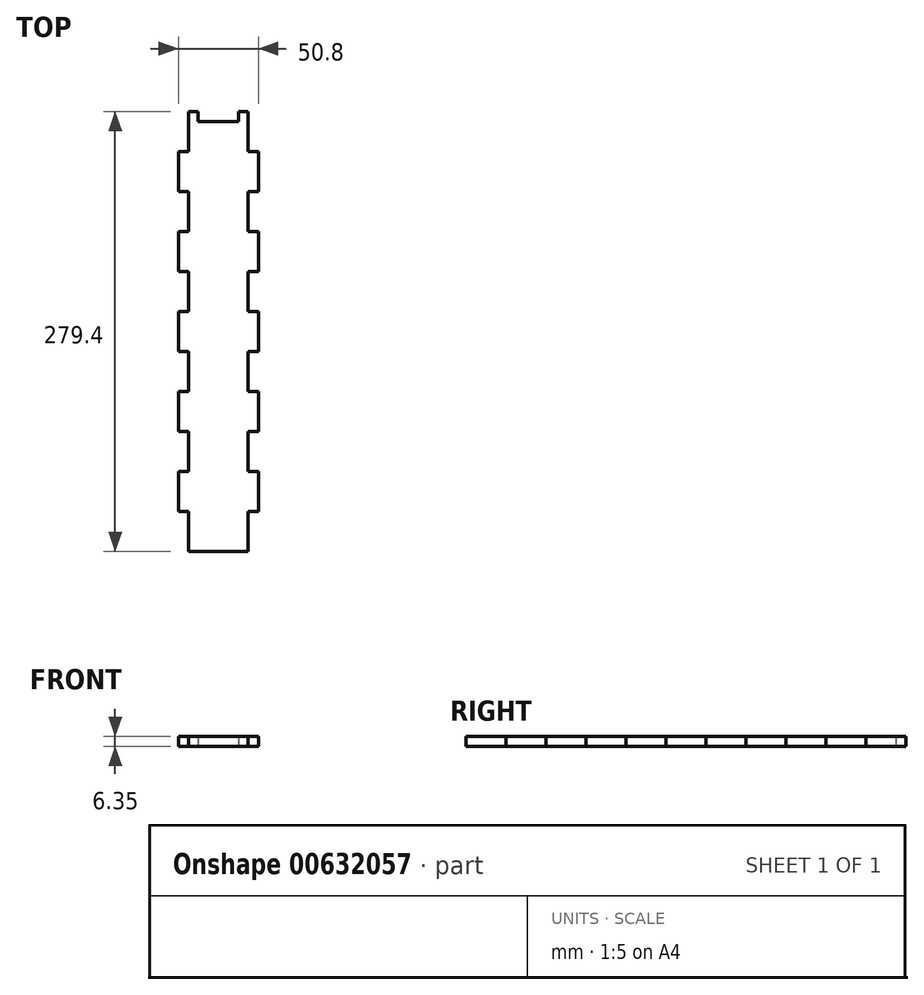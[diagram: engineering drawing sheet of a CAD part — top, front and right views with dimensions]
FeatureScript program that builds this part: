
annotation { "Feature Type Name" : "Feature", "Feature Type Description" : "" }
export const myFeature = defineFeature(function(context is Context, id is Id, definition is map)
    precondition{}
    {
        {
            var Q0;
            Q0=qCreatedBy(makeId("Top.planeOp"),FACE);
            var sketch = newSketch(context, id + "F0", { "sketchPlane" : qUnion([Q0])});
            skLineSegment(sketch, "E0.bottom", {"start": v(0, 279.4) * mm, "end": v(38.1, 279.4) * mm});
            skLineSegment(sketch, "E0.top", {"start": v(0, 0) * mm, "end": v(38.1, 0) * mm});
            skLineSegment(sketch, "E0.left", {"start": v(0, 279.4) * mm, "end": v(0, 0) * mm});
            skLineSegment(sketch, "E0.right", {"start": v(38.1, 279.4) * mm, "end": v(38.1, 0) * mm});
            skSolve(sketch);
        }
        {
            var Q0;
            Q0=qSketchRegion(id+"F0",true);
            extrude(context, id + "F1", {"entities" : qUnion([Q0]), "depth" : 6.35 * mm, "offsetDistance" : 25.4 * mm});
        }
        {
            var Q0;
            Q0=makeQuery(id+"F1.opExtrude","SWEPT_FACE",FACE,{"disambiguationData":[OSD([sQuery(id+"F0.wireOp",EDGE,"E0.right")])]});
            var sketch = newSketch(context, id + "F2", { "sketchPlane" : qUnion([Q0])});
            skLineSegment(sketch, "E1.bottom", {"start": v(0, 6.35) * mm, "end": v(25.4, 6.35) * mm});
            skLineSegment(sketch, "E1.top", {"start": v(0, 0) * mm, "end": v(25.4, 0) * mm});
            skLineSegment(sketch, "E1.left", {"start": v(0, 6.35) * mm, "end": v(0, 0) * mm});
            skLineSegment(sketch, "E1.right", {"start": v(25.4, 6.35) * mm, "end": v(25.4, 0) * mm});
            skLineSegment(sketch, "E2.bottom", {"start": v(25.4, 6.35) * mm, "end": v(50.8, 6.35) * mm});
            skLineSegment(sketch, "E2.top", {"start": v(25.4, 0) * mm, "end": v(50.8, 0) * mm});
            skLineSegment(sketch, "E2.right", {"start": v(50.8, 6.35) * mm, "end": v(50.8, 0) * mm});
            skLineSegment(sketch, "E3.bottom", {"start": v(50.8, 6.35) * mm, "end": v(76.2, 6.35) * mm});
            skLineSegment(sketch, "E3.top", {"start": v(50.8, 0) * mm, "end": v(76.2, 0) * mm});
            skLineSegment(sketch, "E3.right", {"start": v(76.2, 6.35) * mm, "end": v(76.2, 0) * mm});
            skLineSegment(sketch, "E4.bottom", {"start": v(76.2, 6.35) * mm, "end": v(101.6, 6.35) * mm});
            skLineSegment(sketch, "E4.top", {"start": v(76.2, 0) * mm, "end": v(101.6, 0) * mm});
            skLineSegment(sketch, "E4.right", {"start": v(101.6, 6.35) * mm, "end": v(101.6, 0) * mm});
            skLineSegment(sketch, "E5.bottom", {"start": v(101.6, 6.35) * mm, "end": v(127, 6.35) * mm});
            skLineSegment(sketch, "E5.top", {"start": v(101.6, 0) * mm, "end": v(127, 0) * mm});
            skLineSegment(sketch, "E5.right", {"start": v(127, 6.35) * mm, "end": v(127, 0) * mm});
            skLineSegment(sketch, "E6.bottom", {"start": v(127, 6.35) * mm, "end": v(152.4, 6.35) * mm});
            skLineSegment(sketch, "E6.top", {"start": v(127, 0) * mm, "end": v(152.4, 0) * mm});
            skLineSegment(sketch, "E6.right", {"start": v(152.4, 6.35) * mm, "end": v(152.4, 0) * mm});
            skLineSegment(sketch, "E7.bottom", {"start": v(152.4, 6.35) * mm, "end": v(177.8, 6.35) * mm});
            skLineSegment(sketch, "E7.top", {"start": v(152.4, 0) * mm, "end": v(177.8, 0) * mm});
            skLineSegment(sketch, "E7.right", {"start": v(177.8, 6.35) * mm, "end": v(177.8, 0) * mm});
            skLineSegment(sketch, "E8.bottom", {"start": v(177.8, 6.35) * mm, "end": v(203.2, 6.35) * mm});
            skLineSegment(sketch, "E8.top", {"start": v(177.8, 0) * mm, "end": v(203.2, 0) * mm});
            skLineSegment(sketch, "E8.right", {"start": v(203.2, 6.35) * mm, "end": v(203.2, 0) * mm});
            skLineSegment(sketch, "E9.bottom", {"start": v(203.2, 6.35) * mm, "end": v(228.6, 6.35) * mm});
            skLineSegment(sketch, "E9.top", {"start": v(203.2, 0) * mm, "end": v(228.6, 0) * mm});
            skLineSegment(sketch, "E9.right", {"start": v(228.6, 6.35) * mm, "end": v(228.6, 0) * mm});
            skLineSegment(sketch, "E10.bottom", {"start": v(228.6, 6.35) * mm, "end": v(254, 6.35) * mm});
            skLineSegment(sketch, "E10.top", {"start": v(228.6, 0) * mm, "end": v(254, 0) * mm});
            skLineSegment(sketch, "E10.right", {"start": v(254, 6.35) * mm, "end": v(254, 0) * mm});
            skLineSegment(sketch, "E11.bottom", {"start": v(254, 6.35) * mm, "end": v(279.4, 6.35) * mm});
            skLineSegment(sketch, "E11.top", {"start": v(254, 0) * mm, "end": v(279.4, 0) * mm});
            skLineSegment(sketch, "E11.right", {"start": v(279.4, 6.35) * mm, "end": v(279.4, 0) * mm});
            skSolve(sketch);
        }
        {
            var Q0;
            Q0=makeQuery(id+"F1.opExtrude","SWEPT_FACE",FACE,{"disambiguationData":[OSD([sQuery(id+"F0.wireOp",EDGE,"E0.left")])]});
            var sketch = newSketch(context, id + "F3", { "sketchPlane" : qUnion([Q0])});
            skLineSegment(sketch, "E12.bottom", {"start": v(-279.4, 6.35) * mm, "end": v(-254, 6.35) * mm});
            skLineSegment(sketch, "E12.top", {"start": v(-279.4, 0) * mm, "end": v(-254, 0) * mm});
            skLineSegment(sketch, "E12.left", {"start": v(-279.4, 6.35) * mm, "end": v(-279.4, 0) * mm});
            skLineSegment(sketch, "E12.right", {"start": v(-254, 6.35) * mm, "end": v(-254, 0) * mm});
            skLineSegment(sketch, "E13.bottom", {"start": v(-254, 6.35) * mm, "end": v(-228.6, 6.35) * mm});
            skLineSegment(sketch, "E13.top", {"start": v(-254, 0) * mm, "end": v(-228.6, 0) * mm});
            skLineSegment(sketch, "E13.right", {"start": v(-228.6, 6.35) * mm, "end": v(-228.6, 0) * mm});
            skLineSegment(sketch, "E14.bottom", {"start": v(-228.6, 6.35) * mm, "end": v(-203.2, 6.35) * mm});
            skLineSegment(sketch, "E14.top", {"start": v(-228.6, 0) * mm, "end": v(-203.2, 0) * mm});
            skLineSegment(sketch, "E14.right", {"start": v(-203.2, 6.35) * mm, "end": v(-203.2, 0) * mm});
            skLineSegment(sketch, "E15.bottom", {"start": v(-203.2, 6.35) * mm, "end": v(-177.8, 6.35) * mm});
            skLineSegment(sketch, "E15.top", {"start": v(-203.2, 0) * mm, "end": v(-177.8, 0) * mm});
            skLineSegment(sketch, "E15.right", {"start": v(-177.8, 6.35) * mm, "end": v(-177.8, 0) * mm});
            skLineSegment(sketch, "E16.bottom", {"start": v(-177.8, 6.35) * mm, "end": v(-152.4, 6.35) * mm});
            skLineSegment(sketch, "E16.top", {"start": v(-177.8, 0) * mm, "end": v(-152.4, 0) * mm});
            skLineSegment(sketch, "E16.right", {"start": v(-152.4, 6.35) * mm, "end": v(-152.4, 0) * mm});
            skLineSegment(sketch, "E17.bottom", {"start": v(-152.4, 6.35) * mm, "end": v(-127, 6.35) * mm});
            skLineSegment(sketch, "E17.top", {"start": v(-152.4, 0) * mm, "end": v(-127, 0) * mm});
            skLineSegment(sketch, "E17.right", {"start": v(-127, 6.35) * mm, "end": v(-127, 0) * mm});
            skLineSegment(sketch, "E18.bottom", {"start": v(-127, 6.35) * mm, "end": v(-101.6, 6.35) * mm});
            skLineSegment(sketch, "E18.top", {"start": v(-127, 0) * mm, "end": v(-101.6, 0) * mm});
            skLineSegment(sketch, "E18.right", {"start": v(-101.6, 6.35) * mm, "end": v(-101.6, 0) * mm});
            skLineSegment(sketch, "E19.bottom", {"start": v(-101.6, 6.35) * mm, "end": v(-76.2, 6.35) * mm});
            skLineSegment(sketch, "E19.top", {"start": v(-101.6, 0) * mm, "end": v(-76.2, 0) * mm});
            skLineSegment(sketch, "E19.right", {"start": v(-76.2, 6.35) * mm, "end": v(-76.2, 0) * mm});
            skLineSegment(sketch, "E20.bottom", {"start": v(-76.2, 6.35) * mm, "end": v(-50.8, 6.35) * mm});
            skLineSegment(sketch, "E20.top", {"start": v(-76.2, 0) * mm, "end": v(-50.8, 0) * mm});
            skLineSegment(sketch, "E20.right", {"start": v(-50.8, 6.35) * mm, "end": v(-50.8, 0) * mm});
            skLineSegment(sketch, "E21.bottom", {"start": v(-50.8, 6.35) * mm, "end": v(-25.4, 6.35) * mm});
            skLineSegment(sketch, "E21.top", {"start": v(-50.8, 0) * mm, "end": v(-25.4, 0) * mm});
            skLineSegment(sketch, "E21.right", {"start": v(-25.4, 6.35) * mm, "end": v(-25.4, 0) * mm});
            skLineSegment(sketch, "E22.bottom", {"start": v(-25.4, 6.35) * mm, "end": v(0, 6.35) * mm});
            skLineSegment(sketch, "E22.top", {"start": v(-25.4, 0) * mm, "end": v(0, 0) * mm});
            skLineSegment(sketch, "E22.right", {"start": v(0, 6.35) * mm, "end": v(0, 0) * mm});
            skSolve(sketch);
        }
        {
            var Q0;
            Q0=makeQuery(id+"F2.imprint","IMPRINT",FACE,{"disambiguationData":[TD([[makeQuery(id+"F2.imprint","IMPRINT",EDGE,{"derivedFrom":sQuery(id+"F2.wireOp",EDGE,"E10.bottom")}),1.0]])]});
            var Q1;
            Q1=makeQuery(id+"F2.imprint","IMPRINT",FACE,{"disambiguationData":[TD([[makeQuery(id+"F2.imprint","IMPRINT",EDGE,{"derivedFrom":sQuery(id+"F2.wireOp",EDGE,"E8.bottom")}),1.0]])]});
            var Q2;
            Q2=makeQuery(id+"F2.imprint","IMPRINT",FACE,{"disambiguationData":[TD([[makeQuery(id+"F2.imprint","IMPRINT",EDGE,{"derivedFrom":sQuery(id+"F2.wireOp",EDGE,"E6.bottom")}),1.0]])]});
            var Q3;
            Q3=makeQuery(id+"F2.imprint","IMPRINT",FACE,{"disambiguationData":[TD([[makeQuery(id+"F2.imprint","IMPRINT",EDGE,{"derivedFrom":sQuery(id+"F2.wireOp",EDGE,"E4.bottom")}),1.0]])]});
            var Q4;
            Q4=makeQuery(id+"F2.imprint","IMPRINT",FACE,{"disambiguationData":[TD([[makeQuery(id+"F2.imprint","IMPRINT",EDGE,{"derivedFrom":sQuery(id+"F2.wireOp",EDGE,"E2.bottom")}),1.0]])]});
            extrude(context, id + "F4", {"entities" : qUnion([Q0, Q1, Q2, Q3, Q4]), "operationType" : NewBodyOperationType.ADD, "depth" : 6.35 * mm, "offsetDistance" : 25.4 * mm});
        }
        {
            var Q0;
            Q0=makeQuery(id+"F3.imprint","IMPRINT",FACE,{"disambiguationData":[TD([[makeQuery(id+"F3.imprint","IMPRINT",EDGE,{"derivedFrom":sQuery(id+"F3.wireOp",EDGE,"E21.bottom")}),-1.0]])]});
            var Q1;
            Q1=makeQuery(id+"F3.imprint","IMPRINT",FACE,{"disambiguationData":[TD([[makeQuery(id+"F3.imprint","IMPRINT",EDGE,{"derivedFrom":sQuery(id+"F3.wireOp",EDGE,"E19.bottom")}),-1.0]])]});
            var Q2;
            Q2=makeQuery(id+"F3.imprint","IMPRINT",FACE,{"disambiguationData":[TD([[makeQuery(id+"F3.imprint","IMPRINT",EDGE,{"derivedFrom":sQuery(id+"F3.wireOp",EDGE,"E17.bottom")}),-1.0]])]});
            var Q3;
            Q3=makeQuery(id+"F3.imprint","IMPRINT",FACE,{"disambiguationData":[TD([[makeQuery(id+"F3.imprint","IMPRINT",EDGE,{"derivedFrom":sQuery(id+"F3.wireOp",EDGE,"E15.bottom")}),-1.0]])]});
            var Q4;
            Q4=makeQuery(id+"F3.imprint","IMPRINT",FACE,{"disambiguationData":[TD([[makeQuery(id+"F3.imprint","IMPRINT",EDGE,{"derivedFrom":sQuery(id+"F3.wireOp",EDGE,"E13.bottom")}),-1.0]])]});
            extrude(context, id + "F5", {"entities" : qUnion([Q0, Q1, Q2, Q3, Q4]), "operationType" : NewBodyOperationType.ADD, "depth" : 6.35 * mm, "offsetDistance" : 25.4 * mm});
        }
        {
            var Q0;
            Q0=makeQuery(id+"F1.opExtrude","SWEPT_FACE",FACE,{"disambiguationData":[OSD([sQuery(id+"F0.wireOp",EDGE,"E0.bottom")])]});
            var sketch = newSketch(context, id + "F6", { "sketchPlane" : qUnion([Q0])});
            skLineSegment(sketch, "E23.bottom", {"start": v(-38.1, 6.35) * mm, "end": v(-31.75, 6.35) * mm});
            skLineSegment(sketch, "E23.top", {"start": v(-38.1, 0) * mm, "end": v(-31.75, 0) * mm});
            skLineSegment(sketch, "E23.left", {"start": v(-38.1, 6.35) * mm, "end": v(-38.1, 0) * mm});
            skLineSegment(sketch, "E23.right", {"start": v(-31.75, 6.35) * mm, "end": v(-31.75, 0) * mm});
            skLineSegment(sketch, "E24.bottom", {"start": v(0, 6.35) * mm, "end": v(-6.35, 6.35) * mm});
            skLineSegment(sketch, "E24.top", {"start": v(0, 0) * mm, "end": v(-6.35, 0) * mm});
            skLineSegment(sketch, "E24.left", {"start": v(0, 6.35) * mm, "end": v(0, 0) * mm});
            skLineSegment(sketch, "E24.right", {"start": v(-6.35, 6.35) * mm, "end": v(-6.35, 0) * mm});
            skSolve(sketch);
        }
        {
            var Q0;
            {var subQ0=sQuery(id+"F6.wireOp",EDGE,"E23.right");Q0=makeQuery(id+"F6.imprint","IMPRINT",FACE,{"disambiguationData":[TD([[makeQuery(id+"F6.imprint","IMPRINT",EDGE,{"derivedFrom":subQ0}),1.0]])]});}
            extrude(context, id + "F7", {"entities" : qUnion([Q0]), "operationType" : NewBodyOperationType.REMOVE, "oppositeDirection" : true, "depth" : 6.35 * mm, "offsetDistance" : 25.4 * mm});
        }
    });
